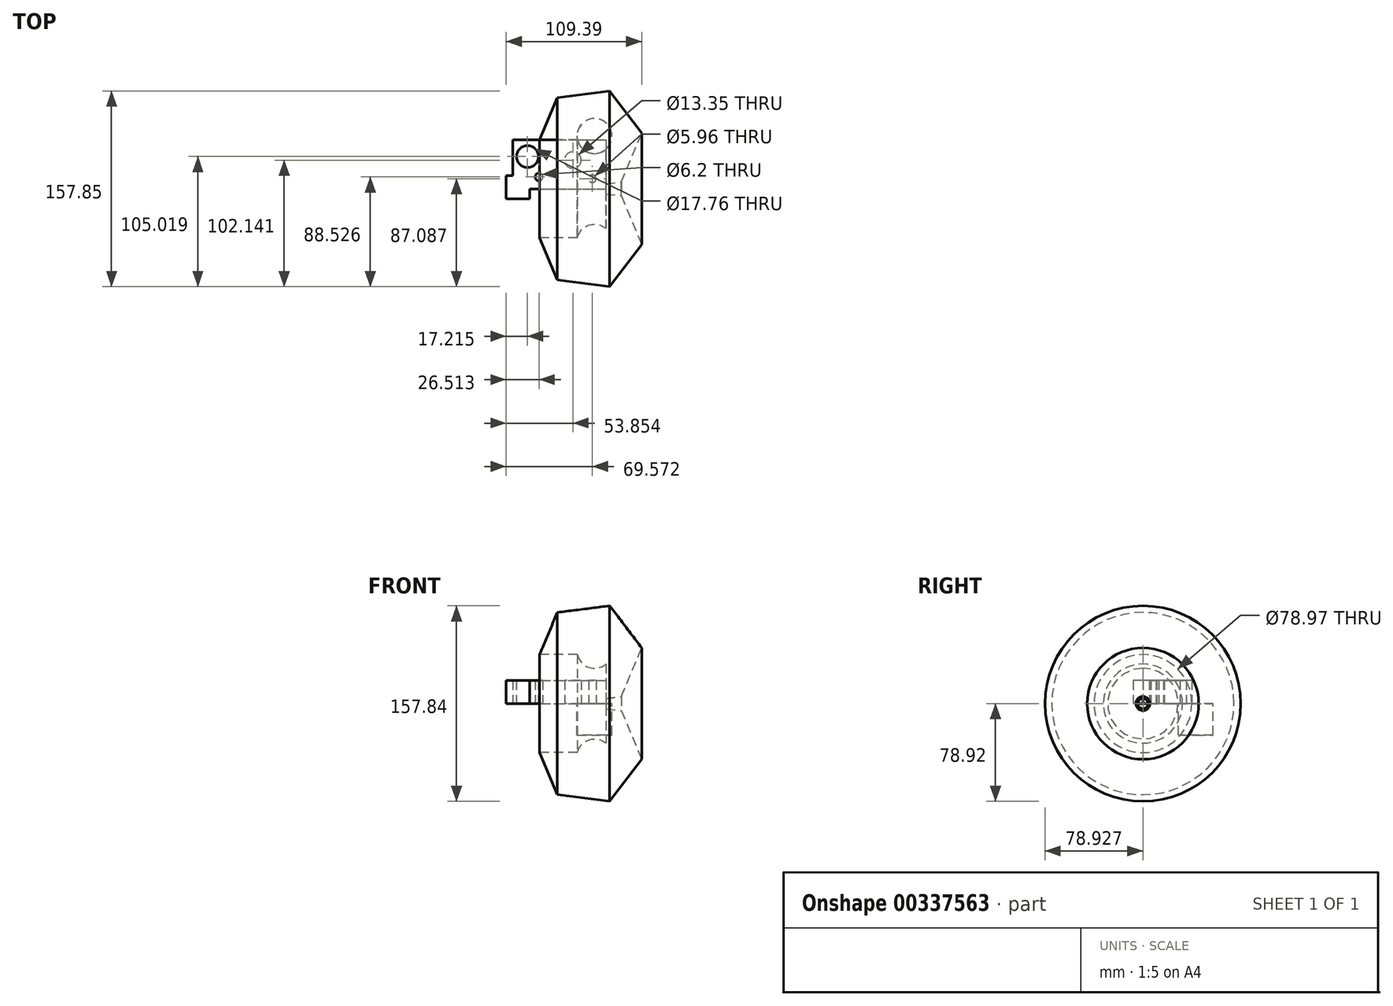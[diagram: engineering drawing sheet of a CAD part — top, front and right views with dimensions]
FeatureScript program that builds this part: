
annotation { "Feature Type Name" : "Feature", "Feature Type Description" : "" }
export const myFeature = defineFeature(function(context is Context, id is Id, definition is map)
    precondition{}
    {
        {
            var Q0;
            Q0=qCreatedBy(makeId("Top.planeOp"),FACE);
            var sketch = newSketch(context, id + "F0", { "sketchPlane" : qUnion([Q0])});
            skLineSegment(sketch, "E0.bottom", {"start": v(-38.88, 15.41) * mm, "end": v(36.26, 15.41) * mm});
            skLineSegment(sketch, "E0.top", {"start": v(-38.88, -24.07) * mm, "end": v(36.26, -24.07) * mm});
            skLineSegment(sketch, "E0.left", {"start": v(-38.88, 15.41) * mm, "end": v(-38.88, -24.07) * mm});
            skLineSegment(sketch, "E0.right", {"start": v(36.26, 15.41) * mm, "end": v(36.26, -24.07) * mm});
            skCircle(sketch, "E1", {"center": v(-27.06, 2.02) * mm, "radius": 8.88 * mm});
            skCircle(sketch, "E2", {"center": v(9.58, -0.86) * mm, "radius": 6.68 * mm});
            skCircle(sketch, "E3", {"center": v(25.3, -15.91) * mm, "radius": 2.98 * mm});
            skCircle(sketch, "E4", {"center": v(-17.76, -14.47) * mm, "radius": 3.1 * mm});
            skLineSegment(sketch, "E5.bottom", {"start": v(-44.27, -13.37) * mm, "end": v(-25.3, -13.37) * mm});
            skLineSegment(sketch, "E5.top", {"start": v(-44.27, -32.05) * mm, "end": v(-25.3, -32.05) * mm});
            skLineSegment(sketch, "E5.left", {"start": v(-44.27, -13.37) * mm, "end": v(-44.27, -32.05) * mm});
            skLineSegment(sketch, "E5.right", {"start": v(-25.3, -13.37) * mm, "end": v(-25.3, -32.05) * mm});
            skSolve(sketch);
        }
        {
            var Q0;
            {var subQ1=sQuery(id+"F0.wireOp",EDGE,"E0.bottom");Q0=makeQuery(id+"F0.imprint","IMPRINT",FACE,{"disambiguationData":[TD([[makeQuery(id+"F0.imprint","IMPRINT",EDGE,{"derivedFrom":subQ1}),-1.0]])]});}
            var Q1;
            {var subQ0=sQuery(id+"F0.wireOp",EDGE,"E5.top");Q1=makeQuery(id+"F0.imprint","IMPRINT",FACE,{"disambiguationData":[TD([[makeQuery(id+"F0.imprint","IMPRINT",EDGE,{"derivedFrom":subQ0}),1.0]])]});}
            var Q2;
            {var subQ0=sQuery(id+"F0.wireOp",EDGE,"E0.left");var subQ1=sQuery(id+"F0.wireOp",EDGE,"E0.top");var subQ2=makeQuery(id+"F0.imprint","INTERSECT",VERTEX,{"derivedFrom":[subQ1,subQ0]});Q2=makeQuery(id+"F0.imprint","IMPRINT",FACE,{"disambiguationData":[TD([[makeQuery(id+"F0.imprint","IMPRINT",EDGE,{"disambiguationData":[TD([[subQ2,-1.0]])],"derivedFrom":subQ1}),1.0]])]});}
            extrude(context, id + "F1", {"entities" : qUnion([Q0, Q1, Q2]), "depth" : 18.54 * mm});
        }
        {
            var Q0;
            Q0=makeQuery(id+"F1.opExtrude","CAP_FACE",FACE,{"disambiguationData":[OSD([sQuery(id+"F0.wireOp",EDGE,"E0.bottom"),sQuery(id+"F0.wireOp",EDGE,"E0.top"),sQuery(id+"F0.wireOp",EDGE,"E0.left"),sQuery(id+"F0.wireOp",EDGE,"E0.right"),sQuery(id+"F0.wireOp",EDGE,"E1"),sQuery(id+"F0.wireOp",EDGE,"E2"),sQuery(id+"F0.wireOp",EDGE,"E3"),sQuery(id+"F0.wireOp",EDGE,"E4"),sQuery(id+"F0.wireOp",EDGE,"E5.bottom"),sQuery(id+"F0.wireOp",EDGE,"E5.top"),sQuery(id+"F0.wireOp",EDGE,"E5.left"),sQuery(id+"F0.wireOp",EDGE,"E5.right")])],"isStart":true});
            var sketch = newSketch(context, id + "F2", { "sketchPlane" : qUnion([Q0])});
            skCircle(sketch, "E6", {"center": v(27.04, -18.56) * mm, "radius": 14.11 * mm});
            skSolve(sketch);
        }
        {
            var Q0;
            Q0 = qSketchRegion(id + "F2", true);
            extrude(context, id + "F3", {"entities" : qUnion([Q0]), "operationType" : NewBodyOperationType.ADD, "depth" : 25.4 * mm});
        }
        {
            var Q0;
            Q0=makeQuery(id+"F1.opExtrude","CAP_FACE",FACE,{"disambiguationData":[OSD([sQuery(id+"F0.wireOp",EDGE,"E0.bottom"),sQuery(id+"F0.wireOp",EDGE,"E0.top"),sQuery(id+"F0.wireOp",EDGE,"E0.left"),sQuery(id+"F0.wireOp",EDGE,"E0.right"),sQuery(id+"F0.wireOp",EDGE,"E1"),sQuery(id+"F0.wireOp",EDGE,"E2"),sQuery(id+"F0.wireOp",EDGE,"E3"),sQuery(id+"F0.wireOp",EDGE,"E4"),sQuery(id+"F0.wireOp",EDGE,"E5.bottom"),sQuery(id+"F0.wireOp",EDGE,"E5.top"),sQuery(id+"F0.wireOp",EDGE,"E5.left"),sQuery(id+"F0.wireOp",EDGE,"E5.right")])],"isStart":true});
            var sketch = newSketch(context, id + "F4", { "sketchPlane" : qUnion([Q0])});
            skSolve(sketch);
        }
        {
            var Q0;
            {var subQ6=sQuery(id+"F0.wireOp",EDGE,"E0.top");Q0=makeQuery(id+"F4.imprint","IMPRINT",FACE,{"disambiguationData":[TD([[makeQuery(id+"F4.imprint","IMPRINT",EDGE,{"derivedFrom":makeQuery(id+"F1.opExtrude","CAP_EDGE",EDGE,{"disambiguationData":[OSD([subQ6])],"isStart":true})}),-1.0]])]});}
            var sketch = newSketch(context, id + "F5", { "sketchPlane" : qUnion([Q0])});
            skCircle(sketch, "E7.cCircle", {"center": v(22.83, -15.54) * mm, "radius": 36.92 * mm, "construction": true});
            skLineSegment(sketch, "E7.0", {"start": v(48.62, 18.41) * mm, "end": v(65.12, -20.9) * mm});
            skLineSegment(sketch, "E7.1", {"start": v(65.12, -20.9) * mm, "end": v(39.33, -54.85) * mm});
            skLineSegment(sketch, "E7.2", {"start": v(39.33, -54.85) * mm, "end": v(-2.97, -49.48) * mm});
            skLineSegment(sketch, "E7.3", {"start": v(-2.97, -49.48) * mm, "end": v(-19.47, -10.17) * mm});
            skLineSegment(sketch, "E7.4", {"start": v(-19.47, -10.17) * mm, "end": v(6.32, 23.78) * mm});
            skLineSegment(sketch, "E7.5", {"start": v(6.32, 23.78) * mm, "end": v(48.62, 18.41) * mm});
            skPoint(sketch, "E7.0.midPoint", {"position": v(56.87, -1.24) * mm});
            skSolve(sketch);
        }
        {
            var Q0;
            Q0=makeQuery(id+"F5.imprint","IMPRINT",FACE,{"disambiguationData":[TD([[makeQuery(id+"F5.imprint","IMPRINT",EDGE,{"derivedFrom":sQuery(id+"F5.wireOp",EDGE,"E7.0")}),-1.0]])]});
            var Q1;
            Q1=makeQuery(id+"F1.opExtrude","CAP_EDGE",EDGE,{"disambiguationData":[OSD([sQuery(id+"F0.wireOp",EDGE,"E0.top")])],"isStart":true});
            revolve(context, id + "F6", {"entities" : qUnion([Q0]), "axis" : qUnion([Q1]), "revolveType" : RevolveType.FULL});
        }
    });
